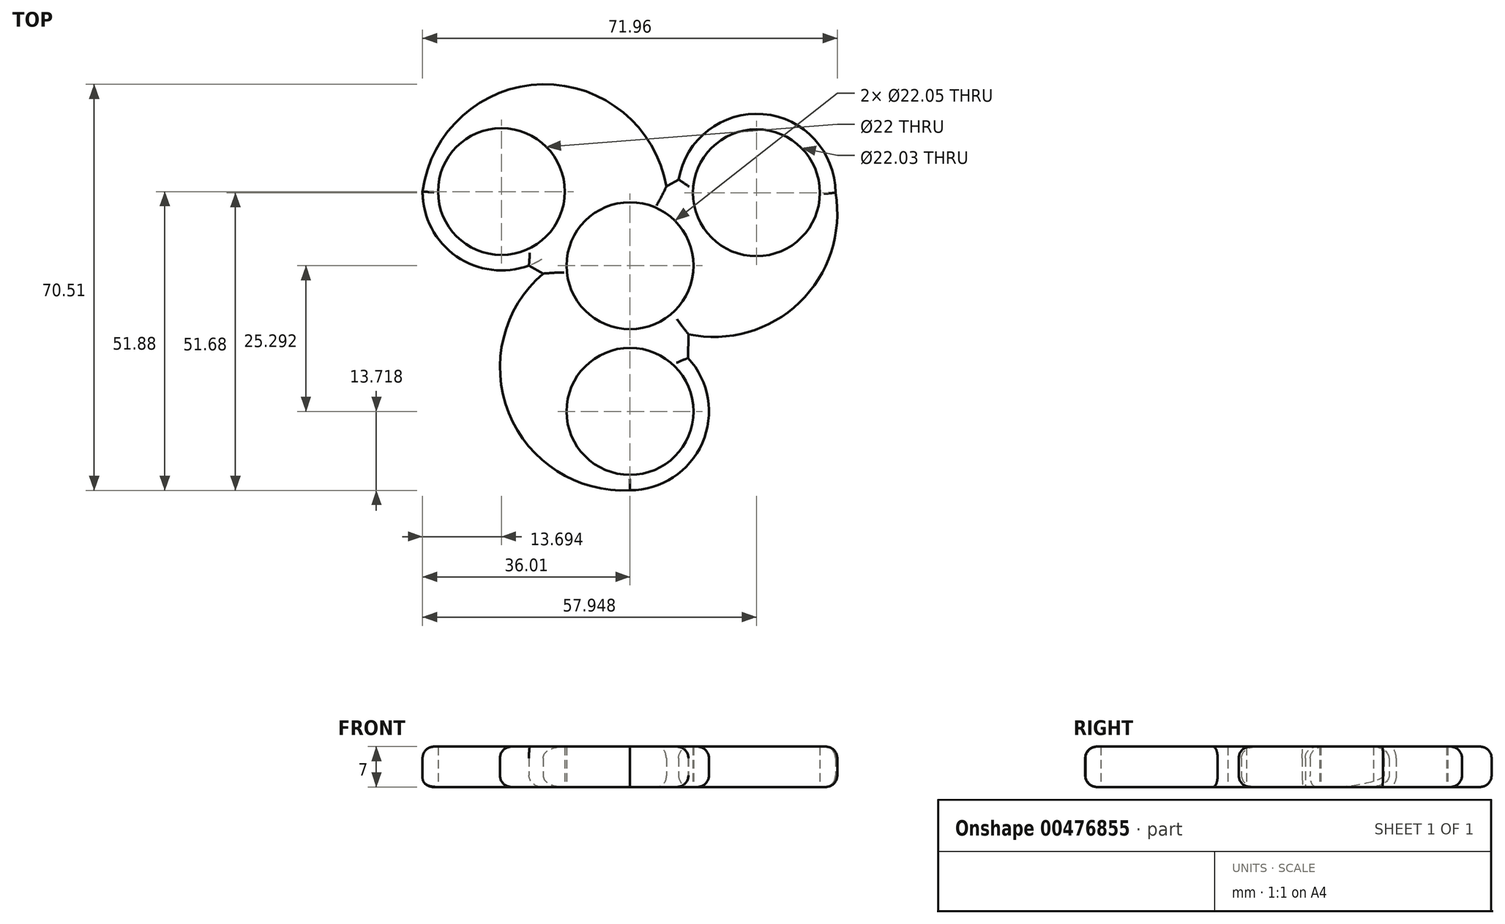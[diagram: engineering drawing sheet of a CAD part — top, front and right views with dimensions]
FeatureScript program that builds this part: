
annotation { "Feature Type Name" : "Feature", "Feature Type Description" : "" }
export const myFeature = defineFeature(function(context is Context, id is Id, definition is map)
    precondition{}
    {
        {
            var Q0;
            Q0=qCreatedBy(makeId("Top.planeOp"),FACE);
            var sketch = newSketch(context, id + "F0", { "sketchPlane" : qUnion([Q0])});
            skPoint(sketch, "E0.0.midPoint", {"position": v(0, 51.52) * mm});
            skCircle(sketch, "E1", {"center": v(0, 0) * mm, "radius": 11.02 * mm});
            skCircle(sketch, "E2", {"center": v(0, -25.3) * mm, "radius": 11.02 * mm});
            skCircle(sketch, "E3", {"center": v(21.94, 12.67) * mm, "radius": 11.01 * mm});
            skCircle(sketch, "E4", {"center": v(-22.32, 12.87) * mm, "radius": 11 * mm});
            skLineSegment(sketch, "E5", {"start": v(10.2, -4.2) * mm, "end": v(10.03, -20.73) * mm});
            skLineSegment(sketch, "E6", {"start": v(-10.2, -4.2) * mm, "end": v(-10.2, -21.09) * mm});
            skLineSegment(sketch, "E7", {"start": v(10.2, -4.2) * mm, "end": v(20.51, 1.75) * mm});
            skLineSegment(sketch, "E8", {"start": v(-10.2, -4.2) * mm, "end": v(-20.88, 1.96) * mm});
            skLineSegment(sketch, "E9", {"start": v(6.6, 13.91) * mm, "end": v(11.76, 16.9) * mm});
            skLineSegment(sketch, "E10", {"start": v(6.6, 13.91) * mm, "end": v(1.43, 10.93) * mm});
            skLineSegment(sketch, "E11", {"start": v(-6.8, 14) * mm, "end": v(-1.43, 10.93) * mm});
            skLineSegment(sketch, "E12", {"start": v(-6.8, 14) * mm, "end": v(-12.16, 17.1) * mm});
            skCircle(sketch, "E13", {"center": v(-22.32, 12.87) * mm, "radius": 13.7 * mm});
            skCircle(sketch, "E14", {"center": v(21.94, 12.67) * mm, "radius": 13.7 * mm});
            skCircle(sketch, "E15", {"center": v(0, -25.3) * mm, "radius": 13.7 * mm});
            skCircle(sketch, "E16", {"center": v(0, 0) * mm, "radius": 13.32 * mm});
            skCircle(sketch, "E17", {"center": v(0, 0) * mm, "radius": 66.48 * mm});
            skArc(sketch, "E18", {"start": v(-13.32, 0) * mm, "mid": v(-21.43, -24.54) * mm, "end": v(0, -38.98) * mm});
            skArc(sketch, "E19", {"start": v(6.55, 11.6) * mm, "mid": v(-14.15, 31.5) * mm, "end": v(-36, 12.87) * mm});
            skArc(sketch, "E20", {"start": v(7.34, -11.11) * mm, "mid": v(28.32, -7.35) * mm, "end": v(35.64, 12.67) * mm});
            skSolve(sketch);
        }
        {
            var Q0;
            {var subQ1=sQuery(id+"F0.wireOp",EDGE,"E7");Q0=makeQuery(id+"F0.imprint","IMPRINT",FACE,{"disambiguationData":[TD([[makeQuery(id+"F0.imprint","IMPRINT",EDGE,{"derivedFrom":subQ1}),1.0]])]});}
            var Q1;
            {var subQ0=sQuery(id+"F0.wireOp",EDGE,"E5");Q1=makeQuery(id+"F0.imprint","IMPRINT",FACE,{"disambiguationData":[TD([[makeQuery(id+"F0.imprint","IMPRINT",EDGE,{"derivedFrom":subQ0}),-1.0]])]});}
            var Q2;
            {var subQ0=sQuery(id+"F0.wireOp",EDGE,"E8");Q2=makeQuery(id+"F0.imprint","IMPRINT",FACE,{"disambiguationData":[TD([[makeQuery(id+"F0.imprint","IMPRINT",EDGE,{"derivedFrom":subQ0}),-1.0]])]});}
            var Q3;
            {var subQ0=sQuery(id+"F0.wireOp",EDGE,"E7");var subQ1=sQuery(id+"F0.wireOp",EDGE,"E3");var subQ2=makeQuery(id+"F0.imprint","INTERSECT",VERTEX,{"derivedFrom":[subQ1,subQ0]});Q3=makeQuery(id+"F0.imprint","IMPRINT",FACE,{"disambiguationData":[TD([[makeQuery(id+"F0.imprint","IMPRINT",EDGE,{"disambiguationData":[TD([[subQ2,-1.0]])],"derivedFrom":subQ1}),-1.0]])]});}
            var Q4;
            {var subQ0=sQuery(id+"F0.wireOp",EDGE,"E8");var subQ1=sQuery(id+"F0.wireOp",EDGE,"E4");var subQ2=makeQuery(id+"F0.imprint","INTERSECT",VERTEX,{"derivedFrom":[subQ1,subQ0]});Q4=makeQuery(id+"F0.imprint","IMPRINT",FACE,{"disambiguationData":[TD([[makeQuery(id+"F0.imprint","IMPRINT",EDGE,{"disambiguationData":[TD([[subQ2,1.0]])],"derivedFrom":subQ1}),-1.0]])]});}
            var Q5;
            {var subQ0=sQuery(id+"F0.wireOp",EDGE,"E5");var subQ1=sQuery(id+"F0.wireOp",EDGE,"E2");var subQ2=makeQuery(id+"F0.imprint","INTERSECT",VERTEX,{"derivedFrom":[subQ1,subQ0]});Q5=makeQuery(id+"F0.imprint","IMPRINT",FACE,{"disambiguationData":[TD([[makeQuery(id+"F0.imprint","IMPRINT",EDGE,{"disambiguationData":[TD([[subQ2,1.0]])],"derivedFrom":subQ1}),-1.0]])]});}
            var Q6;
            {var subQ0=sQuery(id+"F0.wireOp",EDGE,"E10");Q6=makeQuery(id+"F0.imprint","IMPRINT",FACE,{"disambiguationData":[TD([[makeQuery(id+"F0.imprint","IMPRINT",EDGE,{"derivedFrom":subQ0}),1.0]])]});}
            var Q7;
            {var subQ1=sQuery(id+"F0.wireOp",EDGE,"E11");Q7=makeQuery(id+"F0.imprint","IMPRINT",FACE,{"disambiguationData":[TD([[makeQuery(id+"F0.imprint","IMPRINT",EDGE,{"derivedFrom":subQ1}),-1.0]])]});}
            var Q8;
            {var subQ1=sQuery(id+"F0.wireOp",EDGE,"E5");var subQ3=sQuery(id+"F0.wireOp",EDGE,"E16");var subQ4=makeQuery(id+"F0.imprint","INTERSECT",VERTEX,{"derivedFrom":[subQ1,subQ3]});Q8=makeQuery(id+"F0.imprint","IMPRINT",FACE,{"disambiguationData":[TD([[makeQuery(id+"F0.imprint","IMPRINT",EDGE,{"disambiguationData":[TD([[subQ4,-1.0]])],"derivedFrom":subQ3}),1.0]])]});}
            var Q9;
            {var subQ4=sQuery(id+"F0.wireOp",EDGE,"E10");var subQ5=sQuery(id+"F0.wireOp",EDGE,"E1");var subQ6=makeQuery(id+"F0.imprint","INTERSECT",VERTEX,{"derivedFrom":[subQ5,subQ4]});Q9=makeQuery(id+"F0.imprint","IMPRINT",FACE,{"disambiguationData":[TD([[makeQuery(id+"F0.imprint","IMPRINT",EDGE,{"disambiguationData":[TD([[subQ6,1.0]])],"derivedFrom":subQ4}),1.0]])]});}
            var Q10;
            {var subQ0=sQuery(id+"F0.wireOp",EDGE,"E10");var subQ1=sQuery(id+"F0.wireOp",EDGE,"E1");var subQ2=makeQuery(id+"F0.imprint","INTERSECT",VERTEX,{"derivedFrom":[subQ1,subQ0]});Q10=makeQuery(id+"F0.imprint","IMPRINT",FACE,{"disambiguationData":[TD([[makeQuery(id+"F0.imprint","IMPRINT",EDGE,{"disambiguationData":[TD([[subQ2,-1.0]])],"derivedFrom":subQ1}),-1.0]])]});}
            var Q11;
            {var subQ0=sQuery(id+"F0.wireOp",EDGE,"E16");var subQ1=sQuery(id+"F0.wireOp",EDGE,"E13");var subQ2=makeQuery(id+"F0.imprint","INTERSECT",VERTEX,{"disambiguationData":[OD(0.0)],"derivedFrom":[subQ1,subQ0]});Q11=makeQuery(id+"F0.imprint","IMPRINT",FACE,{"disambiguationData":[TD([[makeQuery(id+"F0.imprint","IMPRINT",EDGE,{"disambiguationData":[TD([[subQ2,-1.0]])],"derivedFrom":subQ1}),1.0]])]});}
            var Q12;
            {var subQ4=sQuery(id+"F0.wireOp",EDGE,"E11");var subQ5=sQuery(id+"F0.wireOp",EDGE,"E1");var subQ6=makeQuery(id+"F0.imprint","INTERSECT",VERTEX,{"derivedFrom":[subQ5,subQ4]});Q12=makeQuery(id+"F0.imprint","IMPRINT",FACE,{"disambiguationData":[TD([[makeQuery(id+"F0.imprint","IMPRINT",EDGE,{"disambiguationData":[TD([[subQ6,1.0]])],"derivedFrom":subQ4}),-1.0]])]});}
            var Q13;
            {var subQ1=sQuery(id+"F0.wireOp",EDGE,"E6");var subQ3=sQuery(id+"F0.wireOp",EDGE,"E16");var subQ4=makeQuery(id+"F0.imprint","INTERSECT",VERTEX,{"derivedFrom":[subQ1,subQ3]});Q13=makeQuery(id+"F0.imprint","IMPRINT",FACE,{"disambiguationData":[TD([[makeQuery(id+"F0.imprint","IMPRINT",EDGE,{"disambiguationData":[TD([[subQ4,1.0]])],"derivedFrom":subQ3}),1.0]])]});}
            var Q14;
            {var subQ0=sQuery(id+"F0.wireOp",EDGE,"E16");var subQ1=sQuery(id+"F0.wireOp",EDGE,"E15");var subQ2=makeQuery(id+"F0.imprint","INTERSECT",VERTEX,{"disambiguationData":[OD(0.0)],"derivedFrom":[subQ1,subQ0]});Q14=makeQuery(id+"F0.imprint","IMPRINT",FACE,{"disambiguationData":[TD([[makeQuery(id+"F0.imprint","IMPRINT",EDGE,{"disambiguationData":[TD([[subQ2,-1.0]])],"derivedFrom":subQ1}),-1.0]])]});}
            var Q15;
            {var subQ0=sQuery(id+"F0.wireOp",EDGE,"E16");var subQ1=sQuery(id+"F0.wireOp",EDGE,"E14");var subQ2=makeQuery(id+"F0.imprint","INTERSECT",VERTEX,{"disambiguationData":[OD(0.0)],"derivedFrom":[subQ1,subQ0]});Q15=makeQuery(id+"F0.imprint","IMPRINT",FACE,{"disambiguationData":[TD([[makeQuery(id+"F0.imprint","IMPRINT",EDGE,{"disambiguationData":[TD([[subQ2,-1.0]])],"derivedFrom":subQ1}),1.0]])]});}
            var Q16;
            {var subQ5=sQuery(id+"F0.wireOp",EDGE,"E3");var subQ7=sQuery(id+"F0.wireOp",EDGE,"E7");var subQ8=makeQuery(id+"F0.imprint","INTERSECT",VERTEX,{"derivedFrom":[subQ5,subQ7]});Q16=makeQuery(id+"F0.imprint","IMPRINT",FACE,{"disambiguationData":[TD([[makeQuery(id+"F0.imprint","IMPRINT",EDGE,{"disambiguationData":[TD([[subQ8,1.0]])],"derivedFrom":subQ5}),-1.0]])]});}
            var Q17;
            {var subQ1=sQuery(id+"F0.wireOp",EDGE,"E8");var subQ5=sQuery(id+"F0.wireOp",EDGE,"E4");var subQ6=makeQuery(id+"F0.imprint","INTERSECT",VERTEX,{"derivedFrom":[subQ5,subQ1]});Q17=makeQuery(id+"F0.imprint","IMPRINT",FACE,{"disambiguationData":[TD([[makeQuery(id+"F0.imprint","IMPRINT",EDGE,{"disambiguationData":[TD([[subQ6,-1.0]])],"derivedFrom":subQ5}),-1.0]])]});}
            var Q18;
            {var subQ0=sQuery(id+"F0.wireOp",EDGE,"E16");var subQ1=sQuery(id+"F0.wireOp",EDGE,"E6");var subQ2=makeQuery(id+"F0.imprint","INTERSECT",VERTEX,{"derivedFrom":[subQ1,subQ0]});Q18=makeQuery(id+"F0.imprint","IMPRINT",FACE,{"disambiguationData":[TD([[makeQuery(id+"F0.imprint","IMPRINT",EDGE,{"disambiguationData":[TD([[subQ2,-1.0]])],"derivedFrom":subQ1}),1.0]])]});}
            var Q19;
            {var subQ0=sQuery(id+"F0.wireOp",EDGE,"E16");var subQ1=sQuery(id+"F0.wireOp",EDGE,"E15");var subQ2=makeQuery(id+"F0.imprint","INTERSECT",VERTEX,{"disambiguationData":[OD(0.0)],"derivedFrom":[subQ1,subQ0]});Q19=makeQuery(id+"F0.imprint","IMPRINT",FACE,{"disambiguationData":[TD([[makeQuery(id+"F0.imprint","IMPRINT",EDGE,{"disambiguationData":[TD([[subQ2,-1.0]])],"derivedFrom":subQ1}),1.0]])]});}
            var Q20;
            {var subQ1=sQuery(id+"F0.wireOp",EDGE,"E5");var subQ6=sQuery(id+"F0.wireOp",EDGE,"E2");var subQ9=makeQuery(id+"F0.imprint","INTERSECT",VERTEX,{"derivedFrom":[subQ6,subQ1]});Q20=makeQuery(id+"F0.imprint","IMPRINT",FACE,{"disambiguationData":[TD([[makeQuery(id+"F0.imprint","IMPRINT",EDGE,{"disambiguationData":[TD([[subQ9,-1.0]])],"derivedFrom":subQ6}),-1.0]])]});}
            var Q21;
            {var subQ0=sQuery(id+"F0.wireOp",EDGE,"E16");var subQ1=sQuery(id+"F0.wireOp",EDGE,"E5");var subQ2=makeQuery(id+"F0.imprint","INTERSECT",VERTEX,{"derivedFrom":[subQ1,subQ0]});Q21=makeQuery(id+"F0.imprint","IMPRINT",FACE,{"disambiguationData":[TD([[makeQuery(id+"F0.imprint","IMPRINT",EDGE,{"disambiguationData":[TD([[subQ2,-1.0]])],"derivedFrom":subQ1}),1.0]])]});}
            var Q22;
            {var subQ0=sQuery(id+"F0.wireOp",EDGE,"E16");var subQ1=sQuery(id+"F0.wireOp",EDGE,"E6");var subQ2=makeQuery(id+"F0.imprint","INTERSECT",VERTEX,{"derivedFrom":[subQ1,subQ0]});Q22=makeQuery(id+"F0.imprint","IMPRINT",FACE,{"disambiguationData":[TD([[makeQuery(id+"F0.imprint","IMPRINT",EDGE,{"disambiguationData":[TD([[subQ2,-1.0]])],"derivedFrom":subQ1}),-1.0]])]});}
            var Q23;
            {var subQ3=sQuery(id+"F0.wireOp",EDGE,"E19");var subQ9=sQuery(id+"F0.wireOp",EDGE,"E10");var subQ10=makeQuery(id+"F0.imprint","INTERSECT",VERTEX,{"derivedFrom":[subQ9,subQ3]});Q23=makeQuery(id+"F0.imprint","IMPRINT",FACE,{"disambiguationData":[TD([[makeQuery(id+"F0.imprint","IMPRINT",EDGE,{"disambiguationData":[TD([[subQ10,-1.0]])],"derivedFrom":subQ9}),-1.0]])]});}
            var Q24;
            {var subQ5=sQuery(id+"F0.wireOp",EDGE,"E9");var subQ7=sQuery(id+"F0.wireOp",EDGE,"E10");var subQ8=makeQuery(id+"F0.imprint","INTERSECT",VERTEX,{"derivedFrom":[subQ5,subQ7]});Q24=makeQuery(id+"F0.imprint","IMPRINT",FACE,{"disambiguationData":[TD([[makeQuery(id+"F0.imprint","IMPRINT",EDGE,{"disambiguationData":[TD([[subQ8,-1.0]])],"derivedFrom":subQ5}),-1.0]])]});}
            var Q25;
            {var subQ0=sQuery(id+"F0.wireOp",EDGE,"E18");var subQ1=sQuery(id+"F0.wireOp",EDGE,"E8");var subQ2=makeQuery(id+"F0.imprint","INTERSECT",VERTEX,{"derivedFrom":[subQ1,subQ0]});Q25=makeQuery(id+"F0.imprint","IMPRINT",FACE,{"disambiguationData":[TD([[makeQuery(id+"F0.imprint","IMPRINT",EDGE,{"disambiguationData":[TD([[subQ2,-1.0]])],"derivedFrom":subQ1}),-1.0]])]});}
            var Q26;
            {var subQ0=sQuery(id+"F0.wireOp",EDGE,"E20");var subQ1=sQuery(id+"F0.wireOp",EDGE,"E5");var subQ2=makeQuery(id+"F0.imprint","INTERSECT",VERTEX,{"derivedFrom":[subQ1,subQ0]});Q26=makeQuery(id+"F0.imprint","IMPRINT",FACE,{"disambiguationData":[TD([[makeQuery(id+"F0.imprint","IMPRINT",EDGE,{"disambiguationData":[TD([[subQ2,-1.0]])],"derivedFrom":subQ1}),-1.0]])]});}
            extrude(context, id + "F1", {"entities" : qUnion([Q0, Q1, Q2, Q3, Q4, Q5, Q6, Q7, Q8, Q9, Q10, Q11, Q12, Q13, Q14, Q15, Q16, Q17, Q18, Q19, Q20, Q21, Q22, Q23, Q24, Q25, Q26]), "depth" : 7 * mm});
        }
        {
            var Q0;
            Q0=makeQuery(id+"F1.opExtrude","CAP_EDGE",EDGE,{"disambiguationData":[OSD([sQuery(id+"F0.wireOp",EDGE,"E18")])],"isStart":false});
            var Q1;
            Q1=makeQuery(id+"F1.opExtrude","CAP_EDGE",EDGE,{"disambiguationData":[OSD([sQuery(id+"F0.wireOp",EDGE,"E15")])],"isStart":false});
            var Q2;
            Q2=makeQuery(id+"F1.opExtrude","CAP_EDGE",EDGE,{"disambiguationData":[OSD([sQuery(id+"F0.wireOp",EDGE,"E5")])],"isStart":false});
            var Q3;
            Q3=makeQuery(id+"F1.opExtrude","CAP_EDGE",EDGE,{"disambiguationData":[OSD([sQuery(id+"F0.wireOp",EDGE,"E20")])],"isStart":false});
            var Q4;
            Q4=makeQuery(id+"F1.opExtrude","CAP_EDGE",EDGE,{"disambiguationData":[OSD([sQuery(id+"F0.wireOp",EDGE,"E14")])],"isStart":false});
            var Q5;
            Q5=makeQuery(id+"F1.opExtrude","CAP_EDGE",EDGE,{"disambiguationData":[OSD([sQuery(id+"F0.wireOp",EDGE,"E9")])],"isStart":false});
            var Q6;
            Q6=makeQuery(id+"F1.opExtrude","CAP_EDGE",EDGE,{"disambiguationData":[OSD([sQuery(id+"F0.wireOp",EDGE,"E19")])],"isStart":false});
            var Q7;
            Q7=makeQuery(id+"F1.opExtrude","CAP_EDGE",EDGE,{"disambiguationData":[OSD([sQuery(id+"F0.wireOp",EDGE,"E13")])],"isStart":false});
            var Q8;
            Q8=makeQuery(id+"F1.opExtrude","CAP_EDGE",EDGE,{"disambiguationData":[OSD([sQuery(id+"F0.wireOp",EDGE,"E8")])],"isStart":false});
            var Q9;
            Q9=makeQuery(id+"F1.opExtrude","CAP_EDGE",EDGE,{"disambiguationData":[OSD([sQuery(id+"F0.wireOp",EDGE,"E20")])],"isStart":true});
            var Q10;
            Q10=makeQuery(id+"F1.opExtrude","CAP_EDGE",EDGE,{"disambiguationData":[OSD([sQuery(id+"F0.wireOp",EDGE,"E5")])],"isStart":true});
            var Q11;
            Q11=makeQuery(id+"F1.opExtrude","CAP_EDGE",EDGE,{"disambiguationData":[OSD([sQuery(id+"F0.wireOp",EDGE,"E15")])],"isStart":true});
            var Q12;
            Q12=makeQuery(id+"F1.opExtrude","CAP_EDGE",EDGE,{"disambiguationData":[OSD([sQuery(id+"F0.wireOp",EDGE,"E8")])],"isStart":true});
            var Q13;
            Q13=makeQuery(id+"F1.opExtrude","CAP_EDGE",EDGE,{"disambiguationData":[OSD([sQuery(id+"F0.wireOp",EDGE,"E9")])],"isStart":true});
            var Q14;
            Q14=makeQuery(id+"F1.opExtrude","CAP_EDGE",EDGE,{"disambiguationData":[OSD([sQuery(id+"F0.wireOp",EDGE,"E14")])],"isStart":true});
            var Q15;
            Q15=makeQuery(id+"F1.opExtrude","CAP_EDGE",EDGE,{"disambiguationData":[OSD([sQuery(id+"F0.wireOp",EDGE,"E19")])],"isStart":true});
            fillet(context, id + "F2", {"entities" : qUnion([Q0, Q1, Q2, Q3, Q4, Q5, Q6, Q7, Q8, Q9, Q10, Q11, Q12, Q13, Q14, Q15]), "radius" : 2 * mm, "tangentPropagation" : true, "allowEdgeOverflow" : false});
        }
    });
